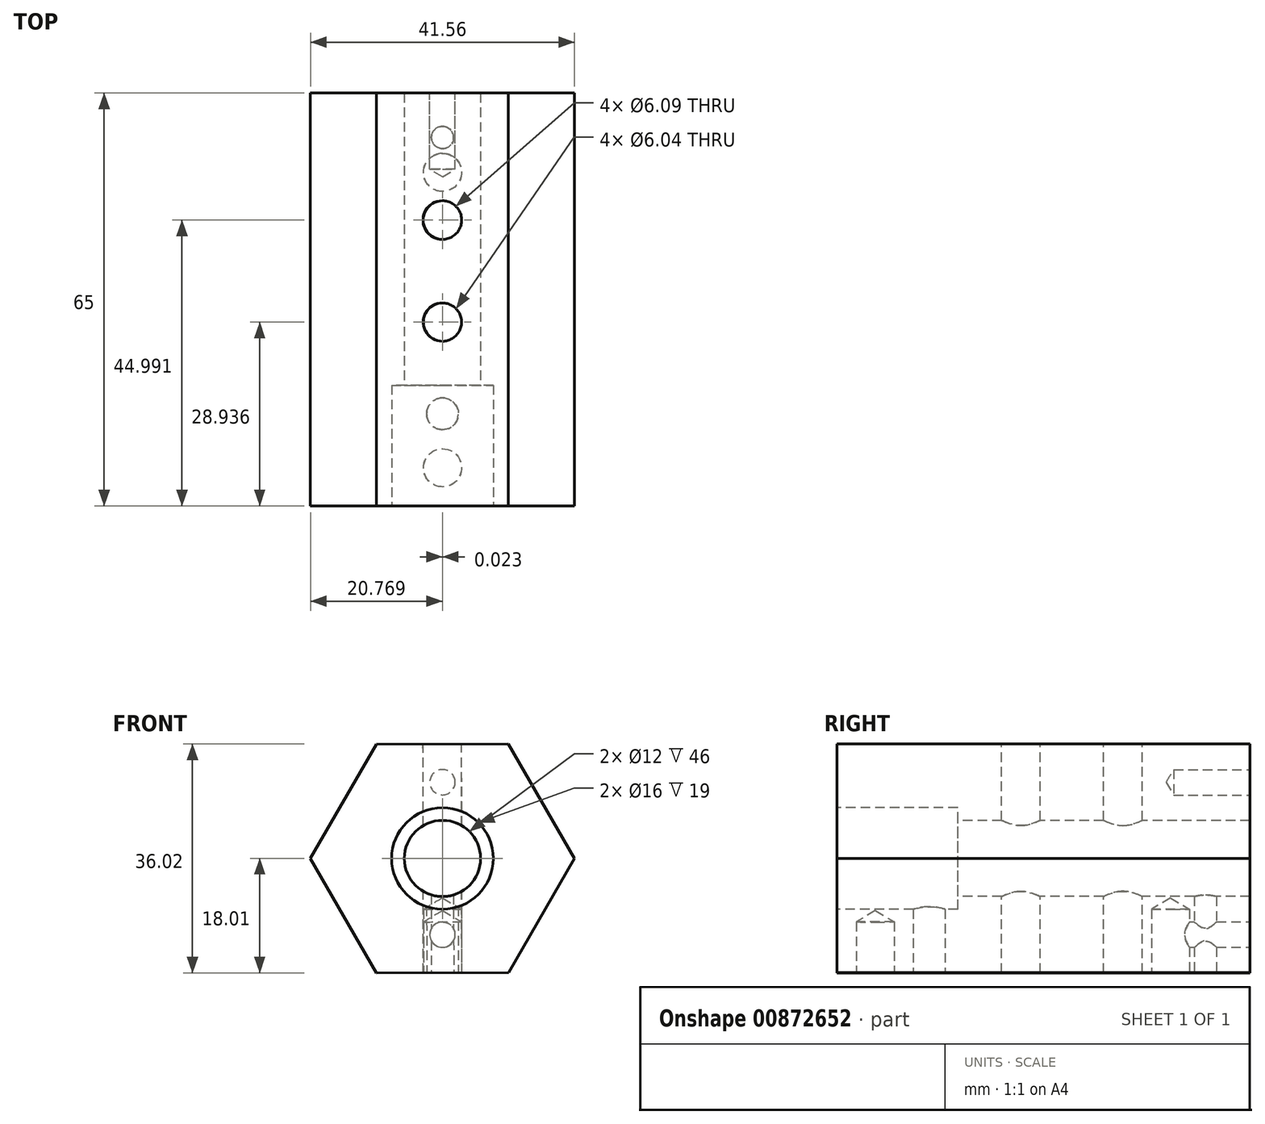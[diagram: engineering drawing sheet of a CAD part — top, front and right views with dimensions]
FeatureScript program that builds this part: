
annotation { "Feature Type Name" : "Feature", "Feature Type Description" : "" }
export const myFeature = defineFeature(function(context is Context, id is Id, definition is map)
    precondition{}
    {
        {
            var Q0;
            Q0=qCreatedBy(makeId("Front.planeOp"),FACE);
            var sketch = newSketch(context, id + "F0", { "sketchPlane" : qUnion([Q0])});
            skCircle(sketch, "E0.cCircle", {"center": v(0, 0) * mm, "radius": 18 * mm, "construction": true});
            skLineSegment(sketch, "E0.0", {"start": v(20.78, 0.02) * mm, "end": v(10.41, -17.99) * mm});
            skLineSegment(sketch, "E0.1", {"start": v(10.41, -17.99) * mm, "end": v(-10.37, -18.01) * mm});
            skLineSegment(sketch, "E0.2", {"start": v(-10.37, -18.01) * mm, "end": v(-20.78, -0.02) * mm});
            skLineSegment(sketch, "E0.3", {"start": v(-20.78, -0.02) * mm, "end": v(-10.41, 17.99) * mm});
            skLineSegment(sketch, "E0.4", {"start": v(-10.41, 17.99) * mm, "end": v(10.37, 18.01) * mm});
            skLineSegment(sketch, "E0.5", {"start": v(10.37, 18.01) * mm, "end": v(20.78, 0.02) * mm});
            skPoint(sketch, "E0.0.midPoint", {"position": v(15.6, -8.98) * mm});
            skSolve(sketch);
        }
        {
            var Q0;
            Q0=makeQuery(id+"F0.imprint","IMPRINT",FACE,{"disambiguationData":[TD([[makeQuery(id+"F0.imprint","IMPRINT",EDGE,{"derivedFrom":sQuery(id+"F0.wireOp",EDGE,"E0.0")}),-1.0]])]});
            extrude(context, id + "F1", {"entities" : qUnion([Q0]), "depth" : 65 * mm, "offsetDistance" : 25 * mm});
        }
        {
            var Q0;
            Q0=makeQuery(id+"F1.opExtrude","CAP_FACE",FACE,{"disambiguationData":[OSD([sQuery(id+"F0.wireOp",EDGE,"E0.0"),sQuery(id+"F0.wireOp",EDGE,"E0.1"),sQuery(id+"F0.wireOp",EDGE,"E0.2"),sQuery(id+"F0.wireOp",EDGE,"E0.3"),sQuery(id+"F0.wireOp",EDGE,"E0.4"),sQuery(id+"F0.wireOp",EDGE,"E0.5")])],"isStart":false});
            var sketch = newSketch(context, id + "F2", { "sketchPlane" : qUnion([Q0])});
            skCircle(sketch, "E1", {"center": v(0, 0) * mm, "radius": 6 * mm});
            skSolve(sketch);
        }
        {
            var Q0;
            Q0=makeQuery(id+"F2.imprint","IMPRINT",FACE,{"disambiguationData":[TD([[makeQuery(id+"F2.imprint","IMPRINT",EDGE,{"derivedFrom":sQuery(id+"F2.wireOp",EDGE,"E1")}),1.0]])]});
            extrude(context, id + "F3", {"entities" : qUnion([Q0]), "operationType" : NewBodyOperationType.REMOVE, "oppositeDirection" : true, "depth" : 65 * mm, "offsetDistance" : 25 * mm});
        }
        {
            var Q0;
            Q0=makeQuery(id+"F1.opExtrude","SWEPT_FACE",FACE,{"disambiguationData":[OSD([sQuery(id+"F0.wireOp",EDGE,"E0.4")])]});
            var sketch = newSketch(context, id + "F4", { "sketchPlane" : qUnion([Q0])});
            skCircle(sketch, "E2", {"center": v(0, -20) * mm, "radius": 3.04 * mm});
            skSolve(sketch);
        }
        {
            var Q0;
            Q0=makeQuery(id+"F4.imprint","IMPRINT",FACE,{"disambiguationData":[TD([[makeQuery(id+"F4.imprint","IMPRINT",EDGE,{"derivedFrom":sQuery(id+"F4.wireOp",EDGE,"E2")}),1.0]])]});
            extrude(context, id + "F5", {"entities" : qUnion([Q0]), "operationType" : NewBodyOperationType.REMOVE, "oppositeDirection" : true, "depth" : 36 * mm, "offsetDistance" : 25 * mm});
        }
        {
            var Q0;
            Q0=makeQuery(id+"F1.opExtrude","SWEPT_FACE",FACE,{"disambiguationData":[OSD([sQuery(id+"F0.wireOp",EDGE,"E0.4")])]});
            var sketch = newSketch(context, id + "F6", { "sketchPlane" : qUnion([Q0])});
            skCircle(sketch, "E3", {"center": v(0, -36.06) * mm, "radius": 3.02 * mm});
            skSolve(sketch);
        }
        {
            var Q0;
            Q0=makeQuery(id+"F6.imprint","IMPRINT",FACE,{"disambiguationData":[TD([[makeQuery(id+"F6.imprint","IMPRINT",EDGE,{"derivedFrom":sQuery(id+"F6.wireOp",EDGE,"E3")}),1.0]])]});
            extrude(context, id + "F7", {"entities" : qUnion([Q0]), "operationType" : NewBodyOperationType.REMOVE, "oppositeDirection" : true, "depth" : 36 * mm, "offsetDistance" : 25 * mm});
        }
        {
            var Q0;
            Q0=makeQuery(id+"F1.opExtrude","SWEPT_FACE",FACE,{"disambiguationData":[OSD([sQuery(id+"F0.wireOp",EDGE,"E0.1")])]});
            var sketch = newSketch(context, id + "F8", { "sketchPlane" : qUnion([Q0])});
            skCircle(sketch, "E4", {"center": v(0, 7) * mm, "radius": 1.75 * mm});
            skSolve(sketch);
        }
        {
            var Q0;
            Q0=makeQuery(id+"F8.imprint","IMPRINT",FACE,{"disambiguationData":[TD([[makeQuery(id+"F8.imprint","IMPRINT",EDGE,{"derivedFrom":sQuery(id+"F8.wireOp",EDGE,"E4")}),1.0]])]});
            extrude(context, id + "F9", {"entities" : qUnion([Q0]), "operationType" : NewBodyOperationType.REMOVE, "oppositeDirection" : true, "depth" : 14 * mm, "offsetDistance" : 25 * mm});
        }
        {
            var Q0;
            Q0=makeQuery(id+"F1.opExtrude","SWEPT_FACE",FACE,{"disambiguationData":[OSD([sQuery(id+"F0.wireOp",EDGE,"E0.1")])]});
            var sketch = newSketch(context, id + "F10", { "sketchPlane" : qUnion([Q0])});
            skCircle(sketch, "E5", {"center": v(0, 50.5) * mm, "radius": 2.5 * mm});
            skSolve(sketch);
        }
        {
            var Q0;
            Q0=makeQuery(id+"F10.imprint","IMPRINT",FACE,{"disambiguationData":[TD([[makeQuery(id+"F10.imprint","IMPRINT",EDGE,{"derivedFrom":sQuery(id+"F10.wireOp",EDGE,"E5")}),1.0]])]});
            extrude(context, id + "F11", {"entities" : qUnion([Q0]), "operationType" : NewBodyOperationType.REMOVE, "oppositeDirection" : true, "depth" : 14 * mm, "offsetDistance" : 25 * mm});
        }
        {
            var Q0;
            Q0=makeQuery(id+"F1.opExtrude","CAP_FACE",FACE,{"disambiguationData":[OSD([sQuery(id+"F0.wireOp",EDGE,"E0.0"),sQuery(id+"F0.wireOp",EDGE,"E0.1"),sQuery(id+"F0.wireOp",EDGE,"E0.2"),sQuery(id+"F0.wireOp",EDGE,"E0.3"),sQuery(id+"F0.wireOp",EDGE,"E0.4"),sQuery(id+"F0.wireOp",EDGE,"E0.5")])],"isStart":false});
            var sketch = newSketch(context, id + "F12", { "sketchPlane" : qUnion([Q0])});
            skCircle(sketch, "E6", {"center": v(0, 0) * mm, "radius": 8 * mm});
            skSolve(sketch);
        }
        {
            var Q0;
            Q0=makeQuery(id+"F12.imprint","IMPRINT",FACE,{"disambiguationData":[TD([[makeQuery(id+"F12.imprint","IMPRINT",EDGE,{"derivedFrom":sQuery(id+"F12.wireOp",EDGE,"E6")}),1.0]])]});
            extrude(context, id + "F13", {"entities" : qUnion([Q0]), "operationType" : NewBodyOperationType.REMOVE, "oppositeDirection" : true, "depth" : 19 * mm, "offsetDistance" : 25 * mm});
        }
        {
            var Q0;
            Q0=makeQuery(id+"F1.opExtrude","CAP_FACE",FACE,{"disambiguationData":[OSD([sQuery(id+"F0.wireOp",EDGE,"E0.0"),sQuery(id+"F0.wireOp",EDGE,"E0.1"),sQuery(id+"F0.wireOp",EDGE,"E0.2"),sQuery(id+"F0.wireOp",EDGE,"E0.3"),sQuery(id+"F0.wireOp",EDGE,"E0.4"),sQuery(id+"F0.wireOp",EDGE,"E0.5")])],"isStart":true});
            var sketch = newSketch(context, id + "F14", { "sketchPlane" : qUnion([Q0])});
            skSolve(sketch);
        }
        {
            var Q0;
            Q0=makeQuery(id+"F14.imprint","IMPRINT",FACE,{"disambiguationData":[TD([[makeQuery(id+"F14.imprint","IMPRINT",EDGE,{"derivedFrom":makeQuery(id+"F1.opExtrude","CAP_EDGE",EDGE,{"disambiguationData":[OSD([sQuery(id+"F0.wireOp",EDGE,"E0.0")])],"isStart":true})}),1.0]])]});
            var sketch = newSketch(context, id + "F15", { "sketchPlane" : qUnion([Q0])});
            skCircle(sketch, "E7", {"center": v(0, 12) * mm, "radius": 2 * mm});
            skSolve(sketch);
        }
        {
            var Q0;
            Q0=sQuery(id+"F15.wireOp",VERTEX,"E7.center");
            var Q1;
            Q1=makeQuery(id+"F1.opExtrude","SWEPT_BODY",BODY,{"disambiguationData":[OSD([sQuery(id+"F0.wireOp",EDGE,"E0.0"),sQuery(id+"F0.wireOp",EDGE,"E0.1"),sQuery(id+"F0.wireOp",EDGE,"E0.2"),sQuery(id+"F0.wireOp",EDGE,"E0.3"),sQuery(id+"F0.wireOp",EDGE,"E0.4"),sQuery(id+"F0.wireOp",EDGE,"E0.5")])]});
            hole(context, id + "F16", {"style" : HoleStyle.SIMPLE, "endStyle" : HoleEndStyle.BLIND, "standardTappedOrClearance" : lookupTablePath({ "standard" : "ISO", "size" : "4", "type" : "Drilled" }), "standardBlindInLast" : lookupTablePath({ "standard" : "ISO", "size" : "4", "type" : "Drilled" }), "holeDiameter" : 4 * mm, "majorDiameter" : 5 * mm, "holeDepth" : 12 * mm, "isTappedThrough" : true, "tappedDepth" : 12 * mm, "tapClearance" : 3, "locations" : qUnion([Q0]), "scope" : qUnion([Q1])});
        }
        {
            var Q0;
            Q0=makeQuery(id+"F14.imprint","IMPRINT",FACE,{"disambiguationData":[TD([[makeQuery(id+"F14.imprint","IMPRINT",EDGE,{"derivedFrom":makeQuery(id+"F1.opExtrude","CAP_EDGE",EDGE,{"disambiguationData":[OSD([sQuery(id+"F0.wireOp",EDGE,"E0.0")])],"isStart":true})}),1.0]])]});
            var sketch = newSketch(context, id + "F17", { "sketchPlane" : qUnion([Q0])});
            skCircle(sketch, "E8", {"center": v(0, -12) * mm, "radius": 1.79 * mm});
            skSolve(sketch);
        }
        {
            var Q0;
            Q0=sQuery(id+"F17.wireOp",VERTEX,"E8.center");
            var Q1;
            Q1=makeQuery(id+"F1.opExtrude","SWEPT_BODY",BODY,{"disambiguationData":[OSD([sQuery(id+"F0.wireOp",EDGE,"E0.0"),sQuery(id+"F0.wireOp",EDGE,"E0.1"),sQuery(id+"F0.wireOp",EDGE,"E0.2"),sQuery(id+"F0.wireOp",EDGE,"E0.3"),sQuery(id+"F0.wireOp",EDGE,"E0.4"),sQuery(id+"F0.wireOp",EDGE,"E0.5")])]});
            hole(context, id + "F18", {"style" : HoleStyle.SIMPLE, "endStyle" : HoleEndStyle.BLIND, "standardTappedOrClearance" : lookupTablePath({ "standard" : "ISO", "size" : "4", "type" : "Drilled" }), "standardBlindInLast" : lookupTablePath({ "standard" : "ISO", "size" : "4", "type" : "Drilled" }), "holeDiameter" : 4 * mm, "majorDiameter" : 5 * mm, "holeDepth" : 12 * mm, "isTappedThrough" : true, "tappedDepth" : 12 * mm, "tapClearance" : 3, "locations" : qUnion([Q0]), "scope" : qUnion([Q1])});
        }
        {
            var Q0;
            Q0=makeQuery(id+"F1.opExtrude","SWEPT_FACE",FACE,{"disambiguationData":[OSD([sQuery(id+"F0.wireOp",EDGE,"E0.1")])]});
            var sketch = newSketch(context, id + "F19", { "sketchPlane" : qUnion([Q0])});
            skLineSegment(sketch, "E9", {"start": v(0, 65) * mm, "end": v(0, 59) * mm});
            skSolve(sketch);
        }
        {
            var Q0;
            Q0=sQuery(id+"F19.wireOp",VERTEX,"E9.end");
            var Q1;
            Q1=makeQuery(id+"F1.opExtrude","SWEPT_BODY",BODY,{"disambiguationData":[OSD([sQuery(id+"F0.wireOp",EDGE,"E0.0"),sQuery(id+"F0.wireOp",EDGE,"E0.1"),sQuery(id+"F0.wireOp",EDGE,"E0.2"),sQuery(id+"F0.wireOp",EDGE,"E0.3"),sQuery(id+"F0.wireOp",EDGE,"E0.4"),sQuery(id+"F0.wireOp",EDGE,"E0.5")])]});
            hole(context, id + "F20", {"style" : HoleStyle.SIMPLE, "endStyle" : HoleEndStyle.BLIND, "standardTappedOrClearance" : lookupTablePath({ "standard" : "ISO", "size" : "6", "type" : "Drilled" }), "standardBlindInLast" : lookupTablePath({ "standard" : "ISO", "size" : "6", "type" : "Drilled" }), "holeDiameter" : 6 * mm, "majorDiameter" : 5 * mm, "holeDepth" : 8 * mm, "isTappedThrough" : true, "tappedDepth" : 12 * mm, "tapClearance" : 3, "locations" : qUnion([Q0]), "scope" : qUnion([Q1])});
        }
        {
            var Q0;
            Q0=makeQuery(id+"F1.opExtrude","SWEPT_FACE",FACE,{"disambiguationData":[OSD([sQuery(id+"F0.wireOp",EDGE,"E0.1")])]});
            var sketch = newSketch(context, id + "F21", { "sketchPlane" : qUnion([Q0])});
            skLineSegment(sketch, "E10", {"start": v(0, 0) * mm, "end": v(0, 12.5) * mm});
            skSolve(sketch);
        }
        {
            var Q0;
            Q0=sQuery(id+"F21.wireOp",VERTEX,"E10.end");
            var Q1;
            Q1=makeQuery(id+"F1.opExtrude","SWEPT_BODY",BODY,{"disambiguationData":[OSD([sQuery(id+"F0.wireOp",EDGE,"E0.0"),sQuery(id+"F0.wireOp",EDGE,"E0.1"),sQuery(id+"F0.wireOp",EDGE,"E0.2"),sQuery(id+"F0.wireOp",EDGE,"E0.3"),sQuery(id+"F0.wireOp",EDGE,"E0.4"),sQuery(id+"F0.wireOp",EDGE,"E0.5")])]});
            hole(context, id + "F22", {"style" : HoleStyle.SIMPLE, "endStyle" : HoleEndStyle.BLIND, "standardTappedOrClearance" : lookupTablePath({ "standard" : "ISO", "size" : "6", "type" : "Drilled" }), "standardBlindInLast" : lookupTablePath({ "standard" : "ISO", "size" : "6", "type" : "Drilled" }), "holeDiameter" : 6 * mm, "majorDiameter" : 5 * mm, "holeDepth" : 10 * mm, "isTappedThrough" : true, "tappedDepth" : 12 * mm, "tapClearance" : 3, "locations" : qUnion([Q0]), "scope" : qUnion([Q1])});
        }
    });
